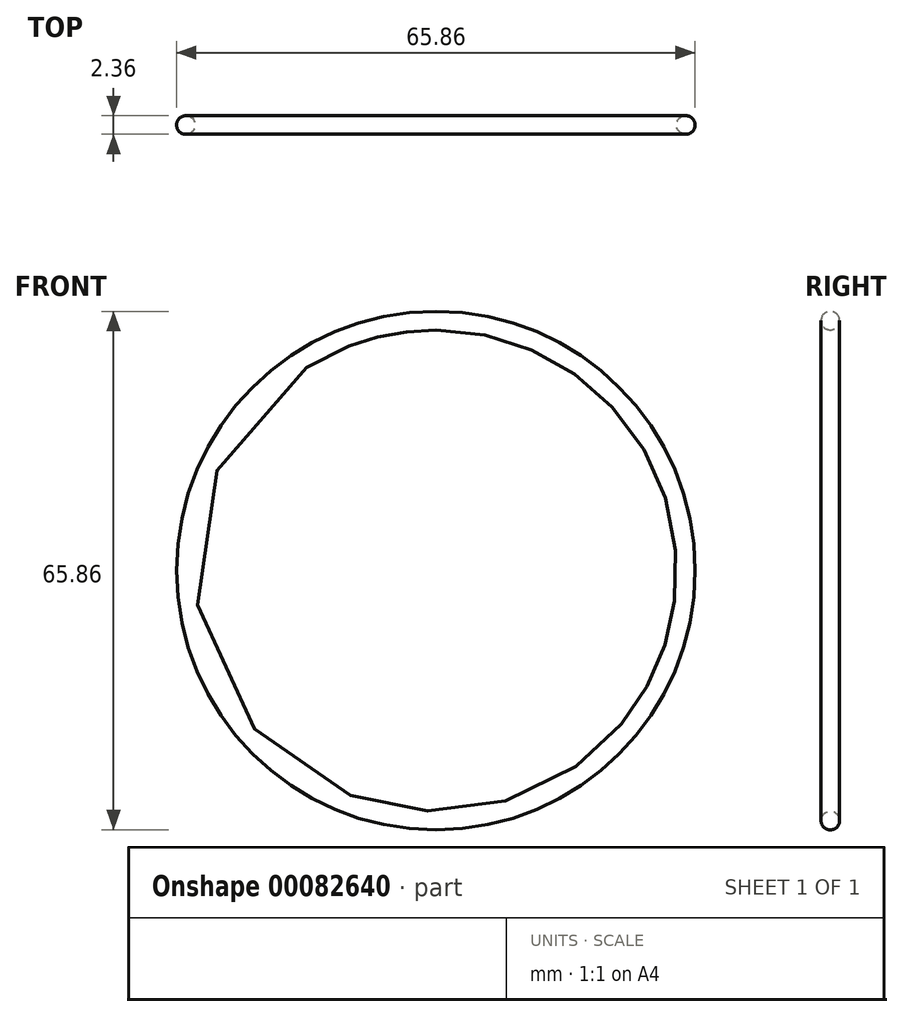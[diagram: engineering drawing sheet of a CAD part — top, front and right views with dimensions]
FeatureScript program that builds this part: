
annotation { "Feature Type Name" : "Feature", "Feature Type Description" : "" }
export const myFeature = defineFeature(function(context is Context, id is Id, definition is map)
    precondition{}
    {
        {
            var Q0;
            Q0=qCreatedBy(makeId("Front.planeOp"),FACE);
            var sketch = newSketch(context, id + "F0", { "sketchPlane" : qUnion([Q0])});
            skCircle(sketch, "E0", {"center": v(0, 0) * mm, "radius": 31.75 * mm});
            skSolve(sketch);
        }
        {
            var Q0;
            Q0=qCreatedBy(makeId("Right.planeOp"),FACE);
            var sketch = newSketch(context, id + "F1", { "sketchPlane" : qUnion([Q0])});
            skPoint(sketch, "E1", {"position": v(0, 31.75) * mm});
            skCircle(sketch, "E2", {"center": v(0, 31.75) * mm, "radius": 1.18 * mm});
            skSolve(sketch);
        }
        {
            var Q0;
            Q0 = qSketchRegion(id + "F1", true);
            var Q1;
            Q1=sQuery(id+"F0.wireOp",EDGE,"E0");
            revolve(context, id + "F2", {"entities" : qUnion([Q0]), "axis" : qUnion([Q1]), "revolveType" : RevolveType.FULL});
        }
    });
